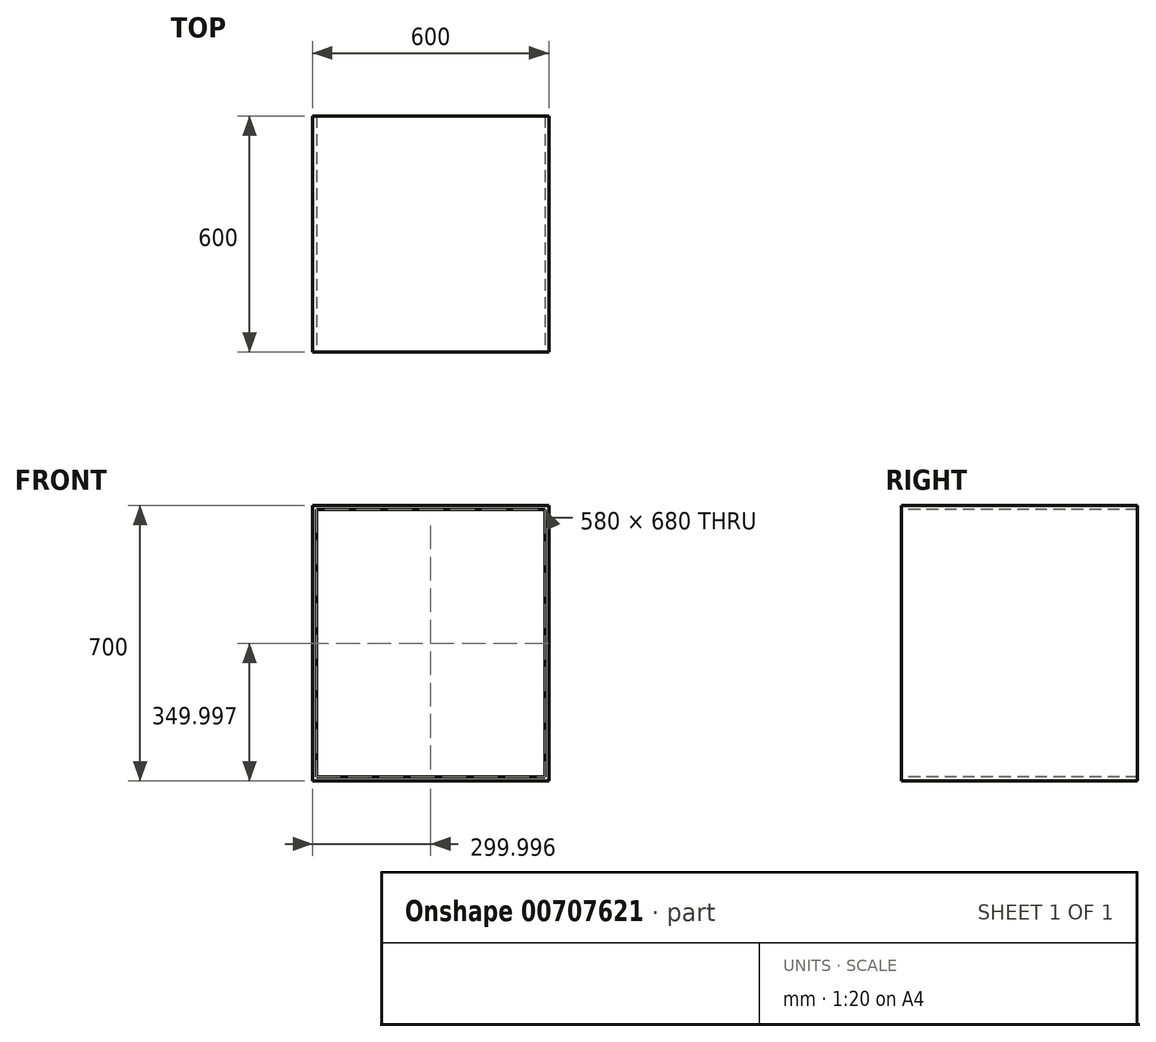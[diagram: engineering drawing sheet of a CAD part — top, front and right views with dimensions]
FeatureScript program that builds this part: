
annotation { "Feature Type Name" : "Feature", "Feature Type Description" : "" }
export const myFeature = defineFeature(function(context is Context, id is Id, definition is map)
    precondition{}
    {
        {
            var Q0;
            Q0=qCreatedBy(makeId("Front.planeOp"),FACE);
            var sketch = newSketch(context, id + "F0", { "sketchPlane" : qUnion([Q0])});
            skLineSegment(sketch, "E0.bottom", {"start": v(-85.56, 589.66) * mm, "end": v(494.44, 589.66) * mm});
            skLineSegment(sketch, "E0.top", {"start": v(-85.56, -90.34) * mm, "end": v(494.44, -90.34) * mm});
            skLineSegment(sketch, "E0.left", {"start": v(-85.56, 589.66) * mm, "end": v(-85.56, -90.34) * mm});
            skLineSegment(sketch, "E0.right", {"start": v(494.44, 589.66) * mm, "end": v(494.44, -90.34) * mm});
            skLineSegment(sketch, "E1.bottom", {"start": v(-95.56, 599.66) * mm, "end": v(504.44, 599.66) * mm});
            skLineSegment(sketch, "E1.top", {"start": v(-95.56, -100.34) * mm, "end": v(504.44, -100.34) * mm});
            skLineSegment(sketch, "E1.left", {"start": v(-95.56, 599.66) * mm, "end": v(-95.56, -100.34) * mm});
            skLineSegment(sketch, "E1.right", {"start": v(504.44, 599.66) * mm, "end": v(504.44, -100.34) * mm});
            skSolve(sketch);
        }
        {
            var Q0;
            Q0=makeQuery(id+"F0.imprint","IMPRINT",FACE,{"disambiguationData":[TD([[makeQuery(id+"F0.imprint","IMPRINT",EDGE,{"derivedFrom":sQuery(id+"F0.wireOp",EDGE,"E0.bottom")}),1.0]])]});
            extrude(context, id + "F1", {"entities" : qUnion([Q0]), "oppositeDirection" : true, "depth" : 600 * mm, "offsetDistance" : 25 * mm});
        }
    });
